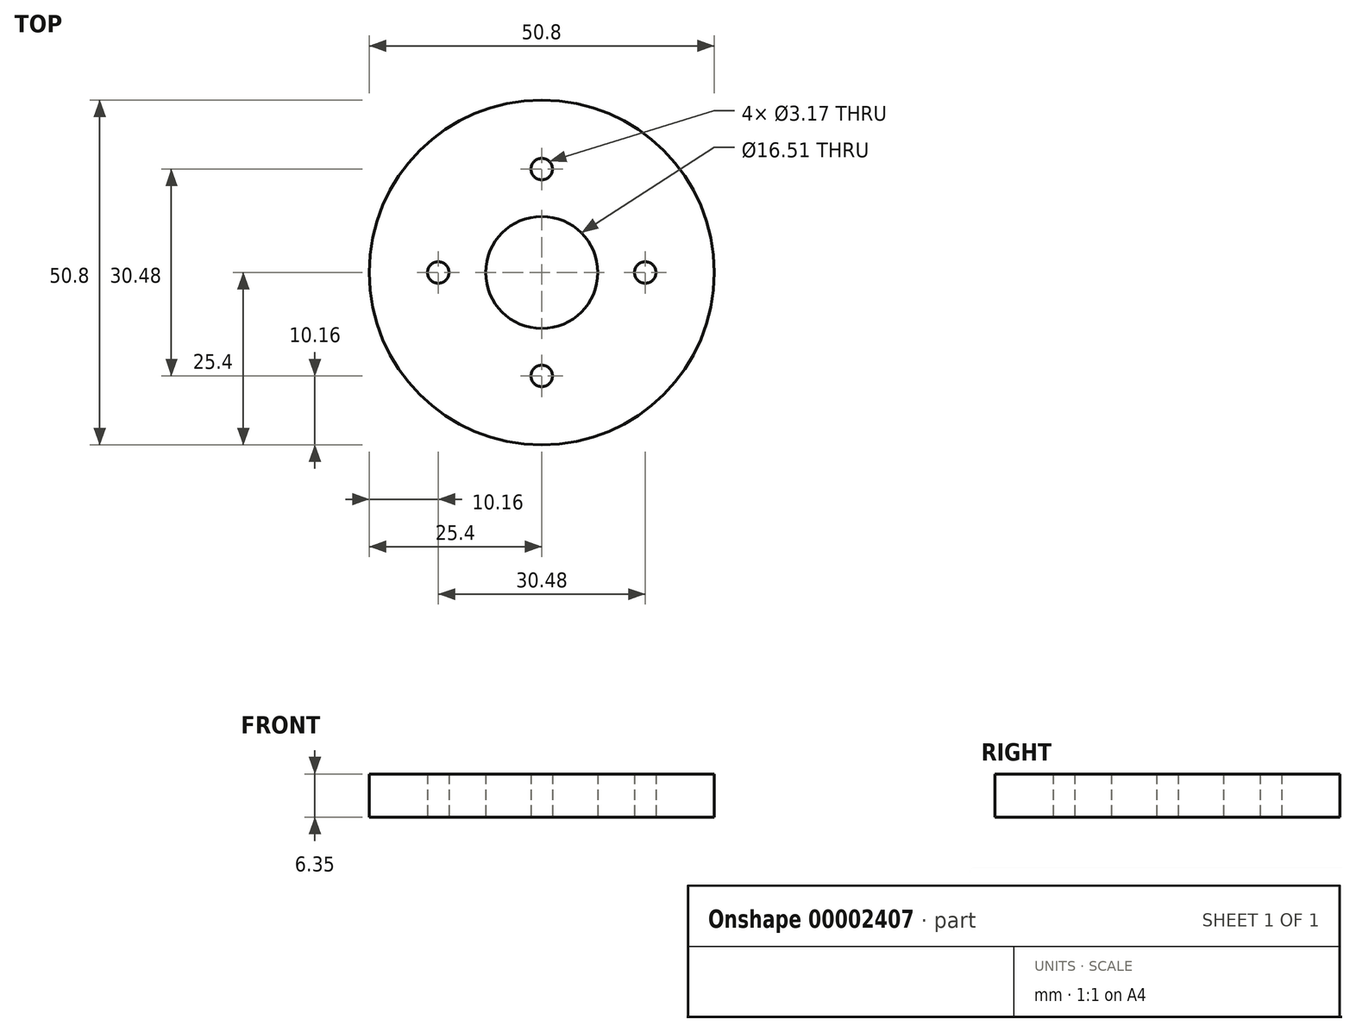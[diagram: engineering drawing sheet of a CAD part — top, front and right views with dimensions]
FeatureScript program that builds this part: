
annotation { "Feature Type Name" : "Feature", "Feature Type Description" : "" }
export const myFeature = defineFeature(function(context is Context, id is Id, definition is map)
    precondition{}
    {
        {
            var Q0;
            Q0=qCreatedBy(makeId("Top.planeOp"),FACE);
            var sketch = newSketch(context, id + "F0", { "sketchPlane" : qUnion([Q0])});
            skCircle(sketch, "E0", {"center": v(0, 0) * mm, "radius": 25.4 * mm});
            skCircle(sketch, "E1", {"center": v(0, 0) * mm, "radius": 8.26 * mm});
            skCircle(sketch, "E2", {"center": v(0, 15.24) * mm, "radius": 1.59 * mm});
            skCircle(sketch, "E3", {"center": v(15.24, 0) * mm, "radius": 1.59 * mm});
            skCircle(sketch, "E4", {"center": v(0, -15.24) * mm, "radius": 1.59 * mm});
            skCircle(sketch, "E5", {"center": v(-15.24, 0) * mm, "radius": 1.59 * mm});
            skSolve(sketch);
        }
        {
            var Q0;
            Q0=qSketchRegion(id+"F0",true);
            extrude(context, id + "F1", {"entities" : qUnion([Q0]), "depth" : 6.35 * mm});
        }
    });
